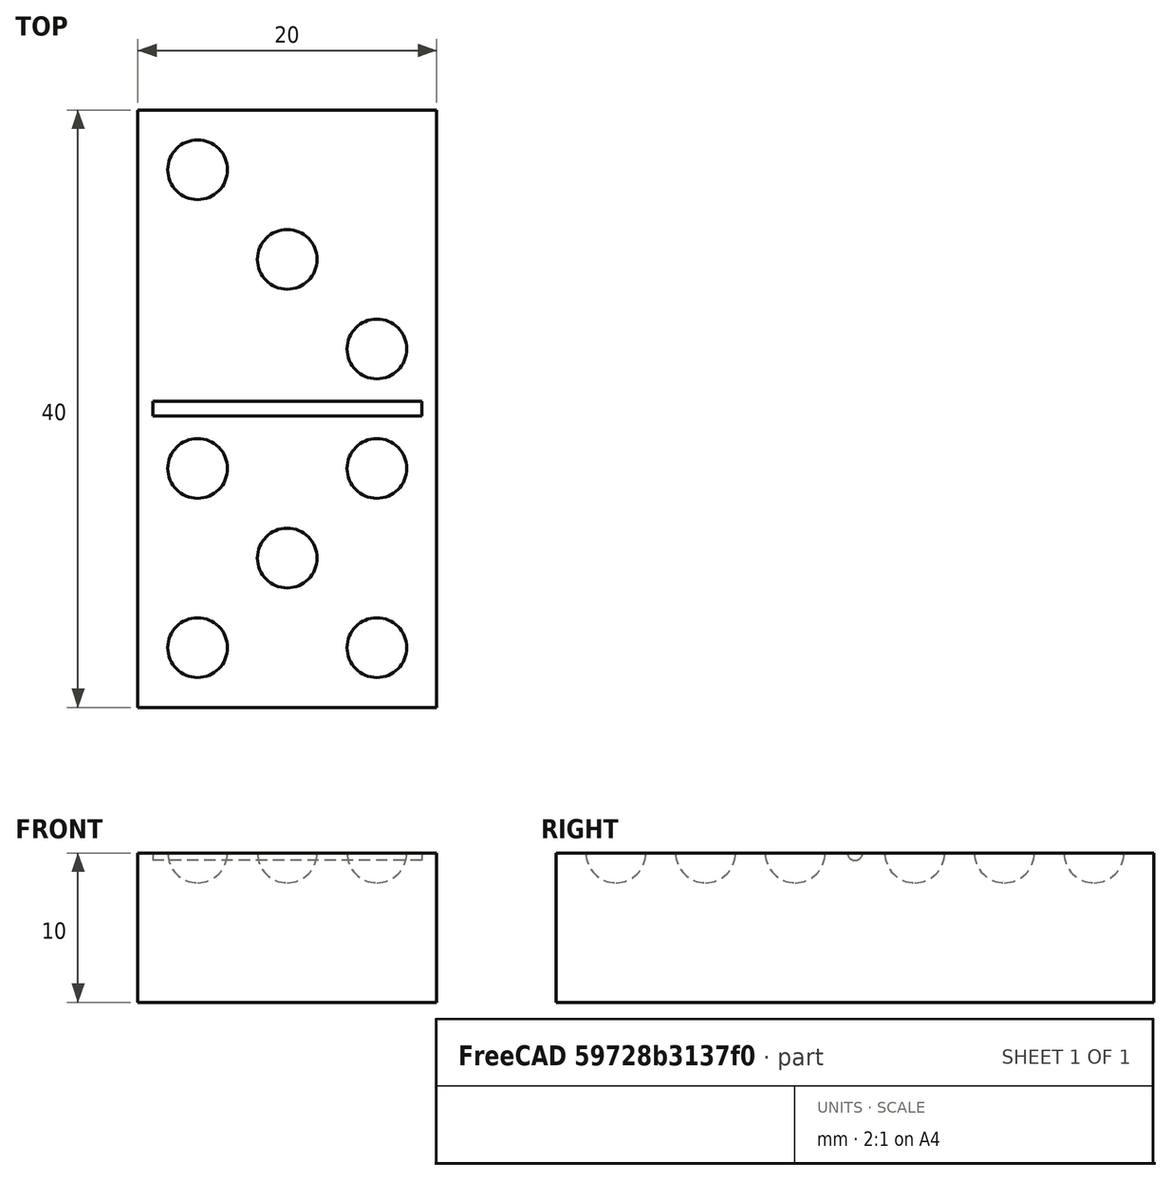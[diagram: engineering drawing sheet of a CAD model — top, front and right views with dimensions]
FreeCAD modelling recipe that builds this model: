
FCSTD DOCUMENT  (FreeCAD 1.0R39285 (Git))
Label: ojt1_t13r03_domino
License: All rights reserved
objects: Part::Sphere×8, Part::Cut×3, Part::MultiFuse×2, Part::Box×1, Part::Cylinder×1
note: 15 computed .brp shape members not serialized (recipe doc carries the construction recipe); baked Part::Feature solids carry a one-line shape summary decoded from their .brp

FEATURE [Part::Box] Box  label="Cub"
  AttacherType = Attacher::AttachEngine3D
  Height = 10
  Length = 20
  Width = 40
FEATURE [Part::Cylinder] Cylinder  label="Cilindre"
  Angle = 360
  AttacherType = Attacher::AttachEngine3D
  FirstAngle = 0
  Height = 18
  Placement = pos=(1,20,10) rot=(0,1,0;1.5708rad)
  Radius = 0.5
  SecondAngle = 0
FEATURE [Part::Sphere] Sphere  label="Esfera"
  Angle1 = -90
  Angle2 = 90
  Angle3 = 360
  AttacherType = Attacher::AttachEngine3D
  Placement = pos=(4,4,10) rot=(0,0,1;0rad)
  Radius = 2
FEATURE [Part::Sphere] Sphere001  label="Esfera001"
  Angle1 = -90
  Angle2 = 90
  Angle3 = 360
  AttacherType = Attacher::AttachEngine3D
  Placement = pos=(16,4,10) rot=(0,0,1;0rad)
  Radius = 2
FEATURE [Part::Sphere] Sphere002  label="Esfera002"
  Angle1 = -90
  Angle2 = 90
  Angle3 = 360
  AttacherType = Attacher::AttachEngine3D
  Placement = pos=(4,16,10) rot=(0,0,1;0rad)
  Radius = 2
FEATURE [Part::Sphere] Sphere003  label="Esfera003"
  Angle1 = -90
  Angle2 = 90
  Angle3 = 360
  AttacherType = Attacher::AttachEngine3D
  Placement = pos=(16,16,10) rot=(0,0,1;0rad)
  Radius = 2
FEATURE [Part::Sphere] Sphere004  label="Esfera004"
  Angle1 = -90
  Angle2 = 90
  Angle3 = 360
  AttacherType = Attacher::AttachEngine3D
  Placement = pos=(10,10,10) rot=(0,0,1;0rad)
  Radius = 2
FEATURE [Part::MultiFuse] Fusion  label="5"
  Refine = true
  Shapes = -> [Sphere,Sphere001,Sphere002,Sphere003,Sphere004]
FEATURE [Part::Sphere] Sphere005  label="Esfera005"
  Angle1 = -90
  Angle2 = 90
  Angle3 = 360
  AttacherType = Attacher::AttachEngine3D
  Placement = pos=(4,36,10) rot=(0,0,1;0rad)
  Radius = 2
FEATURE [Part::Sphere] Sphere006  label="Esfera006"
  Angle1 = -90
  Angle2 = 90
  Angle3 = 360
  AttacherType = Attacher::AttachEngine3D
  Placement = pos=(16,24,10) rot=(0,0,1;0rad)
  Radius = 2
FEATURE [Part::Sphere] Sphere007  label="Esfera007"
  Angle1 = -90
  Angle2 = 90
  Angle3 = 360
  AttacherType = Attacher::AttachEngine3D
  Placement = pos=(10,30,10) rot=(0,0,1;0rad)
  Radius = 2
FEATURE [Part::MultiFuse] Fusion001  label="3"
  Refine = true
  Shapes = -> [Sphere005,Sphere006,Sphere007]
FEATURE [Part::Cut] Cut
  Base = -> Box
  Refine = true
  Tool = -> Cylinder
FEATURE [Part::Cut] Cut001
  Base = -> Cut
  Refine = true
  Tool = -> Fusion
FEATURE [Part::Cut] Cut002  label="domino"
  Base = -> Cut001
  Refine = true
  Tool = -> Fusion001
